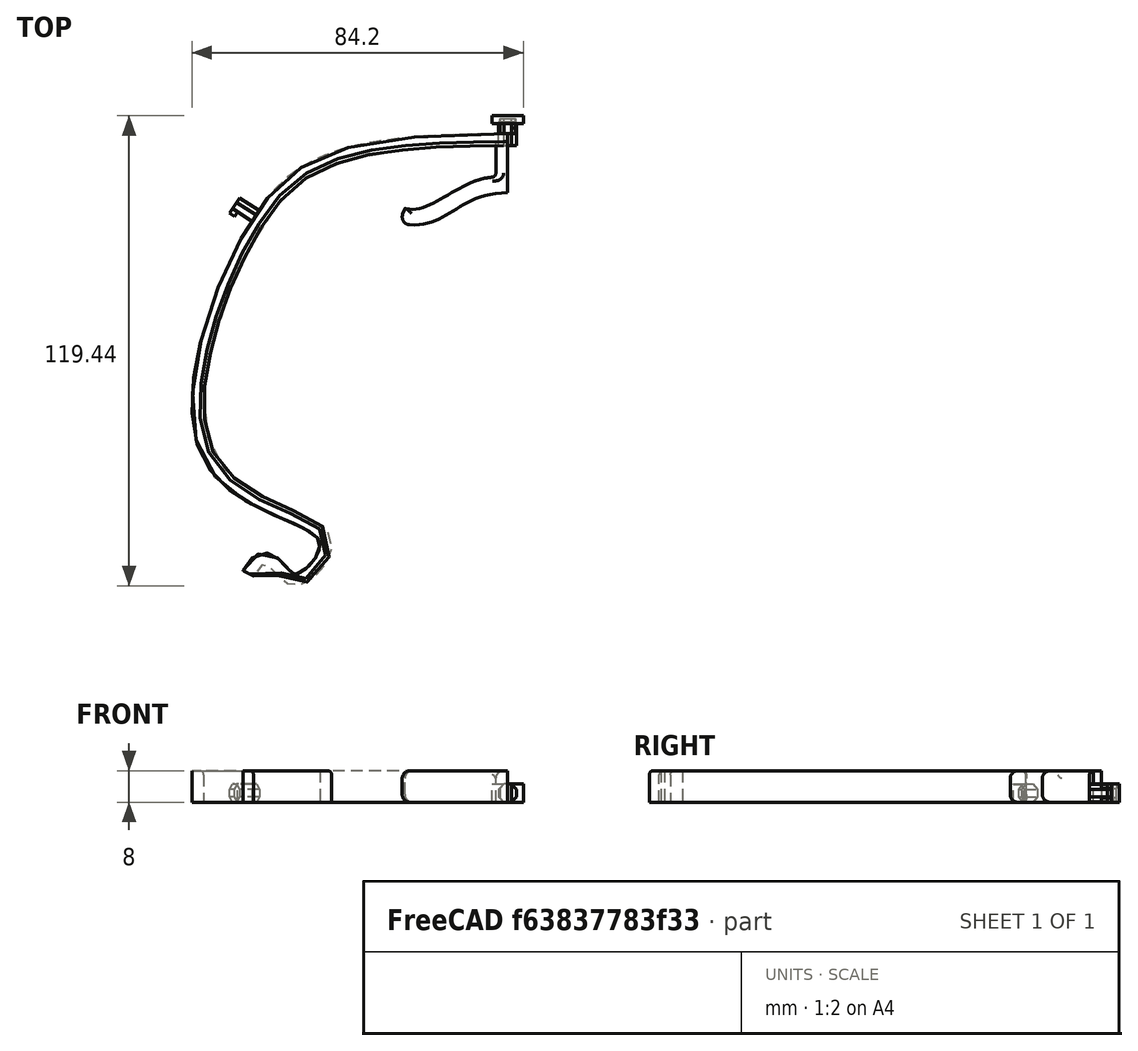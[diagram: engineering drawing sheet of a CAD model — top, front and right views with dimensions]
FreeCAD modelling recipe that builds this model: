
FCSTD DOCUMENT  (FreeCAD 0.18R16146 (Git))
Label: frame-001-01
License: All rights reserved
LicenseURL: http://ja.wikipedia.org/wiki/%E8%91%97%E4%BD%9C%E6%A8%A9%E8%A1%A8%E7%A4%BA
objects: Sketcher::SketchObject×4, Part::Extrusion×4, Part::Box×3, Part::Cut×2, Part::Fillet×2, Mesh::Feature×1, Part::Sweep×1, Part::Compound×1, Part::Mirroring×1, Part::MultiCommon×1
note: 19 computed .brp shape members not serialized (recipe doc carries the construction recipe); baked Part::Feature solids carry a one-line shape summary decoded from their .brp

FEATURE [Sketcher::SketchObject] Sketch  label="Sketch_FrameShape"
  sketch-geometry (15):
    g0-g7: Circle [constr] x8 (B-spline internal-alignment scaffolding for g8; pole/knot coordinates omitted)
    g8: BSplineCurve PolesCount=8 KnotsCount=6 Degree=3 IsPeriodic=0
    g9-g14: GeomPoint [constr] x6 (B-spline internal-alignment scaffolding for g8; pole/knot coordinates omitted)
  constraints (6):
    c: Radius(g0) = 6
    c: Equal(g0, g1-g6) x6
    c: InternalAlignment(g0-g7 -> g8) x8
    c: InternalAlignment(g9-g14 -> g8) x6
    c: Horizontal(g1,g8)
    c: Coincident(g-1,g8)
FEATURE [Sketcher::SketchObject] Sketch001
  Placement = pos=(0,0,0) rot=(0.57735,0.57735,0.57735;2.0944rad)
  sketch-geometry (4):
    g0: LineSegment StartX=0 StartY=8 StartZ=0 EndX=3 EndY=8 EndZ=0
    g1: LineSegment StartX=3 StartY=8 StartZ=0 EndX=3 EndY=0 EndZ=0
    g2: LineSegment StartX=3 StartY=0 StartZ=0 EndX=0 EndY=0 EndZ=0
    g3: LineSegment StartX=0 StartY=0 StartZ=0 EndX=0 EndY=8 EndZ=0
  constraints (12):
    c: Coincident(g0,g1)
    c: Coincident(g1,g2)
    c: Coincident(g2,g3)
    c: Coincident(g3,g0)
    c: Horizontal(g0)
    c: Horizontal(g2)
    c: Vertical(g1)
    c: Vertical(g3)
    c: DistanceX(g0,g0) = 3
    c: DistanceY(g1,g0) = 8
    c: DistanceX(g-1,g2) = 0
    c: PointOnObject(g2,g-1)
FEATURE [Mesh::Feature] cd43cbcc_75a4_11ea_893f_42010a00001e_UM3E_Visor_frame_EUROPE_ISO838_v3  label="cd43cbcc-75a4-11ea-893f-42010a00001e_UM3E_Visor_frame_EUROPE_ISO838_v3"
  Placement = pos=(0,-59,0) rot=(0,0,1;0rad)
FEATURE [Sketcher::SketchObject] Sketch002  label="OctPinSketch"
  Placement = pos=(0,0,0) rot=(1,0,0;1.5708rad)
  sketch-geometry (9):
    g0: LineSegment StartX=2.3097 StartY=1.35299 StartZ=0 EndX=2.3097 EndY=3.26641 EndZ=0
    g1: LineSegment StartX=2.3097 StartY=3.26641 StartZ=0 EndX=0.956709 EndY=4.6194 EndZ=0
    g2: LineSegment StartX=0.956709 StartY=4.6194 StartZ=0 EndX=-0.956709 EndY=4.6194 EndZ=0
    g3: LineSegment StartX=-0.956709 StartY=4.6194 StartZ=0 EndX=-2.3097 EndY=3.26641 EndZ=0
    g4: LineSegment StartX=-2.3097 StartY=3.26641 StartZ=0 EndX=-2.3097 EndY=1.35299 EndZ=0
    g5: LineSegment StartX=-2.3097 StartY=1.35299 StartZ=0 EndX=-0.956709 EndY=0 EndZ=0
    g6: LineSegment StartX=-0.956709 StartY=0 StartZ=0 EndX=0.956709 EndY=0 EndZ=0
    g7: LineSegment StartX=0.956709 StartY=0 StartZ=0 EndX=2.3097 EndY=1.35299 EndZ=0
    g8: Circle [constr] CenterX=0 CenterY=2.3097 CenterZ=0 NormalX=0 NormalY=0 NormalZ=1 AngleXU=0 Radius=2.5
  constraints (21):
    c: Coincident(g0,g1)
    c: Coincident(g1,g2)
    c: Coincident(g2,g3)
    c: Coincident(g3,g4)
    c: Coincident(g4,g5)
    c: Coincident(g5,g6)
    c: Coincident(g6,g7)
    c: Coincident(g7,g0)
    c: Equal(g0, g1-g7) x7
    c: PointOnObject(g0,g8)
    c: PointOnObject(g1,g8)
    c: PointOnObject(g2,g8)
    c: PointOnObject(g3,g8)
    c: PointOnObject(g4,g8)
    c: PointOnObject(g5,g8)
    c: PointOnObject(g6,g8)
    c: PointOnObject(g7,g8)
    c: Distance(g0,g8) = 2.5
    c: Horizontal(g6)
    c: PointOnObject(g8,g-2)
    c: PointOnObject(g6,g-1)
FEATURE [Part::Extrusion] Extrude002  label="OctPin"
  Base = -> Sketch002
  Dir = (0,-1,0)
  DirMode = 2
  FaceMakerClass = Part::FaceMakerBullseye
  LengthFwd = -6
  LengthRev = 0
  Solid = true
  Symmetric = false
FEATURE [Part::Extrusion] Extrude003  label="OctPinFront"
  Base = -> Sketch002
  Dir = (0,-1,0)
  DirMode = 2
  FaceMakerClass = Part::FaceMakerBullseye
  LengthFwd = -6
  LengthRev = 0
  Placement = pos=(0,3,0) rot=(0,0,1;0rad)
  Solid = true
  Symmetric = false
FEATURE [Part::Extrusion] Extrude004  label="OctPin_WNotch_column"
  Base = -> Sketch002
  Dir = (0,-1,0)
  DirMode = 2
  FaceMakerClass = Part::FaceMakerBullseye
  LengthFwd = -6
  LengthRev = 0
  Solid = true
  Symmetric = false
FEATURE [Part::Box] Box008  label="立方体008"
  AttacherType = Attacher::AttachEngine3D
  Height = 6
  Length = 2
  Placement = pos=(1,0,-0.5) rot=(0,0,1;0rad)
  Width = 4.5
FEATURE [Part::Cut] Cut  label="OctPin_WNotch"
  Base = -> Extrude004
  Tool = -> Box008
FEATURE [Part::Cut] Cut001  label="OctPin_WNotchR"
  Base = -> Extrude004
  Placement = pos=(64.3,-18.51,0) rot=(0,0,-1;0.994838rad)
  Tool = -> Box008
FEATURE [Sketcher::SketchObject] Sketch003
  sketch-geometry (18):
    g0: LineSegment StartX=0 StartY=1 StartZ=0 EndX=0 EndY=-12 EndZ=0
    g1: LineSegment StartX=3 StartY=-8 StartZ=0 EndX=3 EndY=1 EndZ=0
    g2: LineSegment StartX=3 StartY=1 StartZ=0 EndX=0 EndY=1 EndZ=0
    g3: LineSegment StartX=26.0991 StartY=-16 StartZ=0 EndX=27.5556 EndY=-19.7254 EndZ=0
    g4-g7: Circle [constr] x4 (B-spline internal-alignment scaffolding for g8; pole/knot coordinates omitted)
    g8: BSplineCurve PolesCount=4 KnotsCount=2 Degree=3 IsPeriodic=0
    g9: GeomPoint [constr] X=3 Y=-8 Z=0
    g10: GeomPoint [constr] X=26.0991 Y=-16 Z=0
    g11-g14: Circle [constr] x4 (B-spline internal-alignment scaffolding for g15; pole/knot coordinates omitted)
    g15: BSplineCurve PolesCount=4 KnotsCount=2 Degree=3 IsPeriodic=0
    g16: GeomPoint [constr] X=0 Y=-12 Z=0
    g17: GeomPoint [constr] X=27.5556 Y=-19.7254 Z=0
  constraints (32):
    c: PointOnObject(g0,g-2)
    c: Vertical(g0)
    c: Vertical(g1)
    c: Coincident(g1,g2)
    c: Coincident(g2,g0)
    c: DistanceX(g0,g1) = 3
    c: Horizontal(g2)
    c: DistanceY(g-1,g0) = 1
    c: DistanceY(g3,g1) = 8
    c: DistanceY(g0,g1) = 4
    c: DistanceY(g0,g-1) = 12
    c: Coincident(g8,g1)
    c: Radius(g4) = 2
    c: Equal(g4,g5)
    c: Equal(g4,g6)
    c: Equal(g4,g7)
    c: Coincident(g8,g3)
    c: InternalAlignment(g4-g7 -> g8) x4
    c: InternalAlignment(g9,g8)
    c: InternalAlignment(g10,g8)
    c: Coincident(g15,g0)
    c: Radius(g11) = 2
    c: Equal(g11,g12)
    c: Equal(g11,g13)
    c: Equal(g11,g14)
    c: Coincident(g15,g3)
    c: InternalAlignment(g11-g14 -> g15) x4
    c: InternalAlignment(g16,g15)
    c: InternalAlignment(g17,g15)
    c: Distance(g3,g3) = 4
    c: Horizontal(g0,g12)
    c: Horizontal(g5,g1)
FEATURE [Part::Extrusion] Extrude
  Base = -> Sketch003
  Dir = (0,0,1)
  DirMode = 2
  FaceMakerClass = Part::FaceMakerBullseye
  LengthFwd = 8
  LengthRev = 0
  Solid = true
  Symmetric = false
FEATURE [Part::Fillet] Fillet  label="AGOATE_R"
  Base = -> Extrude
  Edges = 8 edges: [Edge1 r=1,Edge4 r=2,Edge11 r=2,Edge12 r=2,Edge13 r=2,Edge15 r=2,Edge16 r=2,Edge18 r=1]
FEATURE [Part::Sweep] Sweep  label="Sweep_RightFrame"
  Frenet = false
  Sections = -> [Sketch001]
  Solid = true
  Spine = -> Sketch [Edge1]
  Transition = 1
FEATURE [Part::Fillet] Fillet001  label="Fillet_Sweep_RightFrame"
  Base = -> Sweep
  Edges = 1 edges r=1: [Edge1]
FEATURE [Part::Compound] Compound  label="RightSide"
  Links = -> [Cut001,Fillet,Fillet001]
FEATURE [Part::Mirroring] Part__Mirroring001  label="LeftSide (Mirrored)"
  Base = (0,0,0)
  Normal = (1,0,0)
  Source = -> Compound
FEATURE [Part::Box] Box  label="立方体"
  AttacherType = Attacher::AttachEngine3D
  Height = 10
  Length = 4
  Placement = pos=(-2,2.8,0) rot=(0,0,1;0rad)
  Width = 4
FEATURE [Part::Box] Box010  label="立方体010"
  AttacherType = Attacher::AttachEngine3D
  Height = 4.7
  Length = 8
  Placement = pos=(-4,5.6,0) rot=(0,0,1;0rad)
  Width = 2
FEATURE [Part::MultiCommon] Common  label="Common_FrontPinT"
  Shapes = -> [Extrude003,Box]
